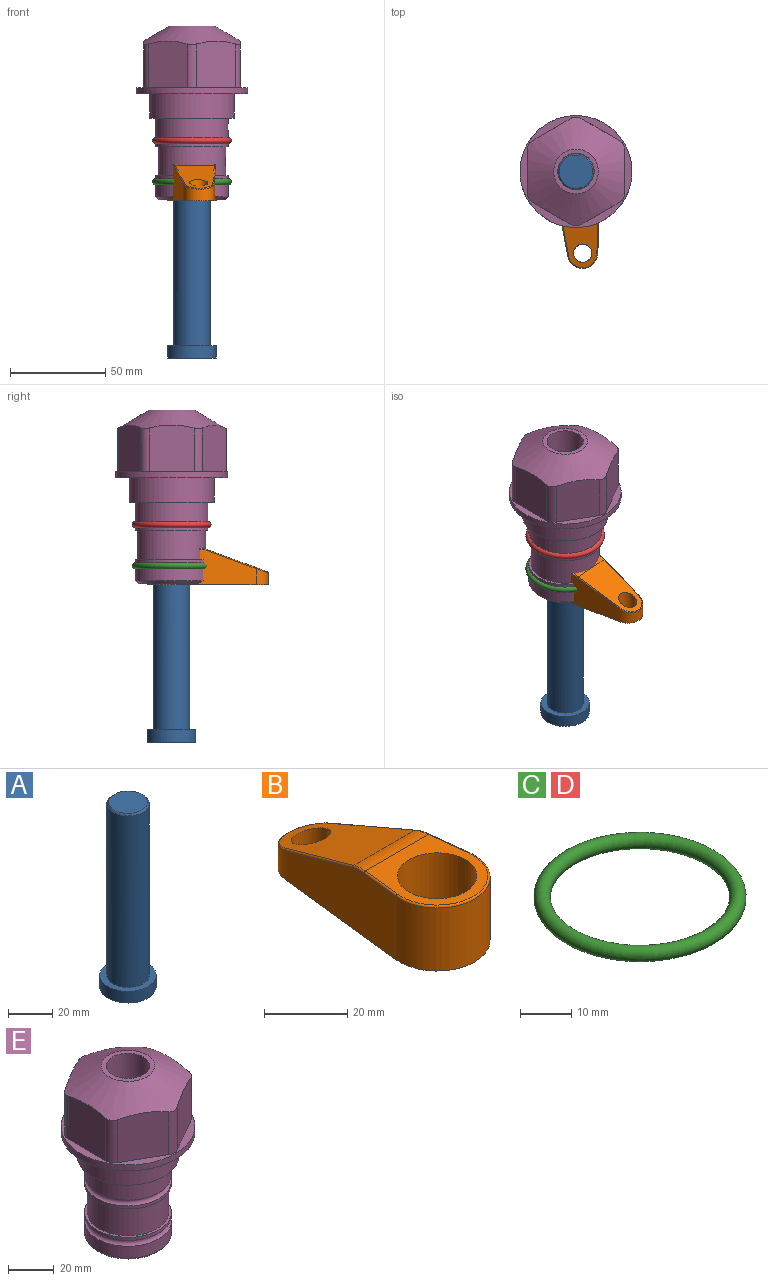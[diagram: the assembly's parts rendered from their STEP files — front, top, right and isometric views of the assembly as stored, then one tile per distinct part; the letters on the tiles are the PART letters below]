
ASSEMBLY  parts=5 mates=3
PART A: 6 faces, bbox 25.4x25.4x101.6 mm
  f0: plane 17.46x17.46mm, normal (0,0,1), area 239.5mm2, adj f5
  f1: plane 25.4x25.4mm, normal (0,0,-1), area 506.7mm2, adj f2
  f2: cylinder r=12.7mm len=25.4mm, axis (0,0,1), area 506.7mm2, adj f1,f3
  f3: plane 25.4x25.4mm, normal (0,0,1), area 221.7mm2, adj f2,f4
  f4: cylinder r=9.53mm len=94.46mm, axis (0,0,1), area 5653mm2, adj f3,f5
  f5: cone r=8.73mm half-angle=45deg, axis (0,0,-1), area 64.4mm2, adj f0,f4
PART B: 44 faces, bbox 27.5x64.5x19.1 mm
  f0: plane 2.3x0.95mm, normal (0,0,-1), area 1mm2, adj f25,f30,f34
  f1: plane 63.5x25.4mm, normal (0,0,-1), area 561.7mm2, adj f2,f3,f4,f5,f6,f7,f19,f20
  f2: cylinder r=12.7mm len=25.4mm, axis (0,0,-1), area 792.2mm2, adj f1,f3,f5,f13
  f3: plane 42.33x18.54mm, normal (0.99,0.11,0), area 647mm2, adj f1,f2,f4,f11,f12,f14
  f4: cylinder r=7.94mm len=15.78mm, axis (0,0,-1), area 158.6mm2, adj f1,f3,f5,f16
  f5: plane 42.33x18.54mm, normal (-0.99,0.11,0), area 647mm2, adj f1,f2,f4,f15,f17,f18
  f6: cylinder r=9.53mm len=19.05mm, axis (0,0,-1), area 1140.1mm2, adj f1,f8
  f7: cylinder r=4.76mm len=10.98mm, axis (0,0,-1), area 276.1mm2, adj f1,f9
  f8: plane 25.83x24.38mm, normal (0,0,1), area 262.2mm2, adj f6,f10,f11,f13,f15
  f9: plane 32.49x20.55mm, normal (0,0.34,0.94), area 489.9mm2, adj f7,f10,f14,f16,f18
  f10: cylinder r=12.7mm len=21.49mm, axis (-1,0,0), area 93.2mm2, adj f8,f9,f12,f17
  f11: cylinder r=0.51mm len=12.34mm, axis (0.11,-0.99,0), area 9.9mm2, adj f3,f8,f12,f13
  f12: bspline ~7.62x1.64mm, area 3.5mm2, adj f3,f10,f11,f14
  f13: torus R=12.19mm, axis (0,0,1), area 33.6mm2, adj f2,f8,f11,f15
  f14: cylinder r=0.51mm len=26.01mm, axis (0.1,-0.93,0.34), area 21.6mm2, adj f3,f9,f12,f16
  f15: cylinder r=0.51mm len=12.34mm, axis (0.11,0.99,0), area 9.9mm2, adj f5,f8,f13,f17
  f16: bspline ~15.78x7.05mm, area 15.7mm2, adj f4,f9,f14,f18
  f17: bspline ~7.62x1.64mm, area 3.5mm2, adj f5,f10,f15,f18
  f18: cylinder r=0.51mm len=26.01mm, axis (0.1,0.93,-0.34), area 21.6mm2, adj f5,f9,f16,f17
  f19: plane 21.6x14.29mm, normal (-0.99,-0.11,0), area 242.6mm2, adj f1,f26,f28,f34,f36,f38
  f20: plane 21.6x14.29mm, normal (0.99,-0.11,0), area 242.6mm2, adj f1,f27,f29,f37,f39,f41
  f21: cylinder r=12.7mm len=14.29mm, axis (0,0,-1), area 173.2mm2, adj f1,f26,f27,f30,f31,f33
  f22: cylinder r=7.94mm len=7.63mm, axis (0,0,-1), area 53.8mm2, adj f1,f28,f29,f42
  f23: plane 2.3x0.95mm, normal (0,0,-1), area 1mm2, adj f25,f33,f37
  f24: plane 17.94x12.32mm, normal (0,-0.34,-0.94), area 191.2mm2, adj f25,f38,f41,f42
  f25: cylinder r=9.53mm len=12.93mm, axis (-1,0,0), area 37.5mm2, adj f0,f23,f24,f31,f36,f39
  f26: cylinder r=1.59mm len=14.29mm, axis (0,0,-1), area 49mm2, adj f1,f19,f21,f32
  f27: cylinder r=1.59mm len=14.29mm, axis (0,0,-1), area 49mm2, adj f1,f20,f21,f35
  f28: cylinder r=1.59mm len=7.28mm, axis (0,0,-1), area 22.1mm2, adj f1,f19,f22,f40
  f29: cylinder r=1.59mm len=7.28mm, axis (0,0,-1), area 22.1mm2, adj f1,f20,f22,f43
  f30: torus R=14.29mm, axis (0,0,1), area 5.8mm2, adj f0,f21,f31,f32
  f31: bspline ~11.06x2.73mm, area 20.8mm2, adj f21,f25,f30,f33
  f32: sphere r=1.59mm, area 5.4mm2, adj f26,f30,f34
  f33: torus R=14.29mm, axis (0,0,1), area 5.8mm2, adj f21,f23,f31,f35
  f34: cylinder r=1.59mm len=1.68mm, axis (-0.11,0.99,0), area 2.4mm2, adj f0,f19,f32,f36
  f35: sphere r=1.59mm, area 5.4mm2, adj f27,f33,f37
  f36: bspline ~5.82x2.33mm, area 7.7mm2, adj f19,f25,f34,f38
  f37: cylinder r=1.59mm len=1.68mm, axis (0.11,0.99,0), area 2.4mm2, adj f20,f23,f35,f39
  f38: cylinder r=1.59mm len=18.33mm, axis (0.1,-0.93,0.34), area 46.7mm2, adj f19,f24,f36,f40
  f39: bspline ~5.82x2.33mm, area 7.7mm2, adj f20,f25,f37,f41
  f40: sphere r=1.59mm, area 3.6mm2, adj f28,f38,f42
  f41: cylinder r=1.59mm len=18.33mm, axis (0.1,0.93,-0.34), area 46.7mm2, adj f20,f24,f39,f43
  f42: bspline ~8.31x1.84mm, area 15.3mm2, adj f22,f24,f40,f43
  f43: sphere r=1.59mm, area 3.6mm2, adj f29,f41,f42
PART C: 1 faces, bbox 44.7x44.7x3.2 mm
  f0: torus R=19.05mm, axis (0,0,1), area 1193.9mm2
PART D: same geometry as C
PART E: 36 faces, bbox 58.7x58.7x91.2 mm
  f0: cylinder r=17.78mm len=35.56mm, axis (0,0,1), area 1670.8mm2, adj f23,f24,f31
  f1: cylinder r=19.05mm len=38.1mm, axis (0,0,1), area 1191.9mm2, adj f26,f27,f30
  f2: plane 58.66x58.66mm, normal (0,0,-1), area 1150.6mm2, adj f3,f28
  f3: cylinder r=29.33mm len=58.66mm, axis (0,0,-1), area 585.1mm2, adj f2,f4
  f4: plane 58.66x58.66mm, normal (0,0,1), area 475.9mm2, adj f3,f5,f6,f7,f8,f9,f10,f11
  f5: plane 24.5x20.32mm, normal (-0.5,0.87,0), area 562.8mm2, adj f4,f15,f16,f17
  f6: plane 24.5x20.32mm, normal (0.5,0.87,0), area 562.8mm2, adj f4,f14,f15,f17
  f7: plane 24.5x23.48mm, normal (1,0,0), area 562.8mm2, adj f4,f13,f14,f17
  f8: plane 24.5x20.32mm, normal (0.5,-0.87,0), area 562.8mm2, adj f4,f12,f13,f17
  f9: plane 24.5x20.32mm, normal (-0.5,-0.87,0), area 562.8mm2, adj f4,f11,f12,f17
  f10: plane 24.5x23.48mm, normal (-1,0,0), area 562.8mm2, adj f4,f11,f16,f17
  f11: cylinder r=5.08mm len=23.01mm, axis (0,0,-1), area 121.2mm2, adj f4,f9,f10,f17
  f12: cylinder r=5.08mm len=23.01mm, axis (0,0,-1), area 121.2mm2, adj f4,f8,f9,f17
  f13: cylinder r=5.08mm len=23.01mm, axis (0,0,-1), area 121.2mm2, adj f4,f7,f8,f17
  f14: cylinder r=5.08mm len=23.01mm, axis (0,0,-1), area 121.2mm2, adj f4,f6,f7,f17
  f15: cylinder r=5.08mm len=23.01mm, axis (0,0,-1), area 121.2mm2, adj f4,f5,f6,f17
  f16: cylinder r=5.08mm len=23.01mm, axis (0,0,-1), area 121.2mm2, adj f4,f5,f10,f17
  f17: cone r=11.73mm half-angle=60deg, axis (0,0,-1), area 2071.8mm2, adj f5,f6,f7,f8,f9,f10,f11,f12
  f18: plane 23.46x23.46mm, normal (0,0,1), area 147.4mm2, adj f17,f35
  f19: plane 34.93x34.93mm, normal (0,0,-1), area 958mm2, adj f29
  f20: cylinder r=19.05mm len=38.1mm, axis (0,0,1), area 760.1mm2, adj f21,f29
  f21: torus R=19.05mm, axis (0,0,1), area 565.3mm2, adj f20,f22
  f22: cylinder r=19.05mm len=38.1mm, axis (0,0,1), area 190mm2, adj f21,f23
  f23: plane 38.1x38.1mm, normal (0,0,1), area 146.9mm2, adj f0,f22
  f24: plane 38.1x38.1mm, normal (0,0,-1), area 146.9mm2, adj f0,f25
  f25: cylinder r=19.05mm len=38.1mm, axis (0,0,1), area 190mm2, adj f24,f26
  f26: torus R=19.05mm, axis (0,0,1), area 565.3mm2, adj f1,f25
  f27: plane 44.45x44.45mm, normal (0,0,-1), area 411.7mm2, adj f1,f28
  f28: cylinder r=22.23mm len=44.45mm, axis (0,0,1), area 1773.5mm2, adj f2,f27
  f29: cone r=19.05mm half-angle=45deg, axis (0,0,1), area 257.5mm2, adj f19,f20
  f30: cylinder r=3.17mm len=6.75mm, axis (-1,0,0), area 128mm2, adj f1,f33
  f31: cylinder r=3.17mm len=6.35mm, axis (-1,0,0), area 102.5mm2, adj f0,f33
  f32: plane 25.4x25.4mm, normal (0,0,1), area 506.7mm2, adj f33
  f33: cylinder r=12.7mm len=66.42mm, axis (0,0,-1), area 5236.2mm2, adj f30,f31,f32,f34
  f34: cone r=9.53mm half-angle=30deg, axis (0,0,-1), area 443.4mm2, adj f33,f35
  f35: cylinder r=9.53mm len=19.05mm, axis (0,0,-1), area 849mm2, adj f18,f34
PLACE A rot(axis=(0,0,-1),85.3deg) t=(0,0,-110.56)mm
PLACE B rot(axis=(0,0,-1),175.3deg) t=(0,0,-55.95)mm
PLACE C t=(0,0,-21.59)mm
PLACE D at identity
PLACE E at identity fixed
MATE fastened C.f0 <-> E.f0  axis (0,0,1) through (0,0,-46.1)mm
MATE cylindrical A.f2 <-> E.f0  axis (0,0,1) through (0,0,-84.92)mm
MATE fastened B.f2 <-> A.f2  axis (0,0,1) through (0,0,-36.9)mm
